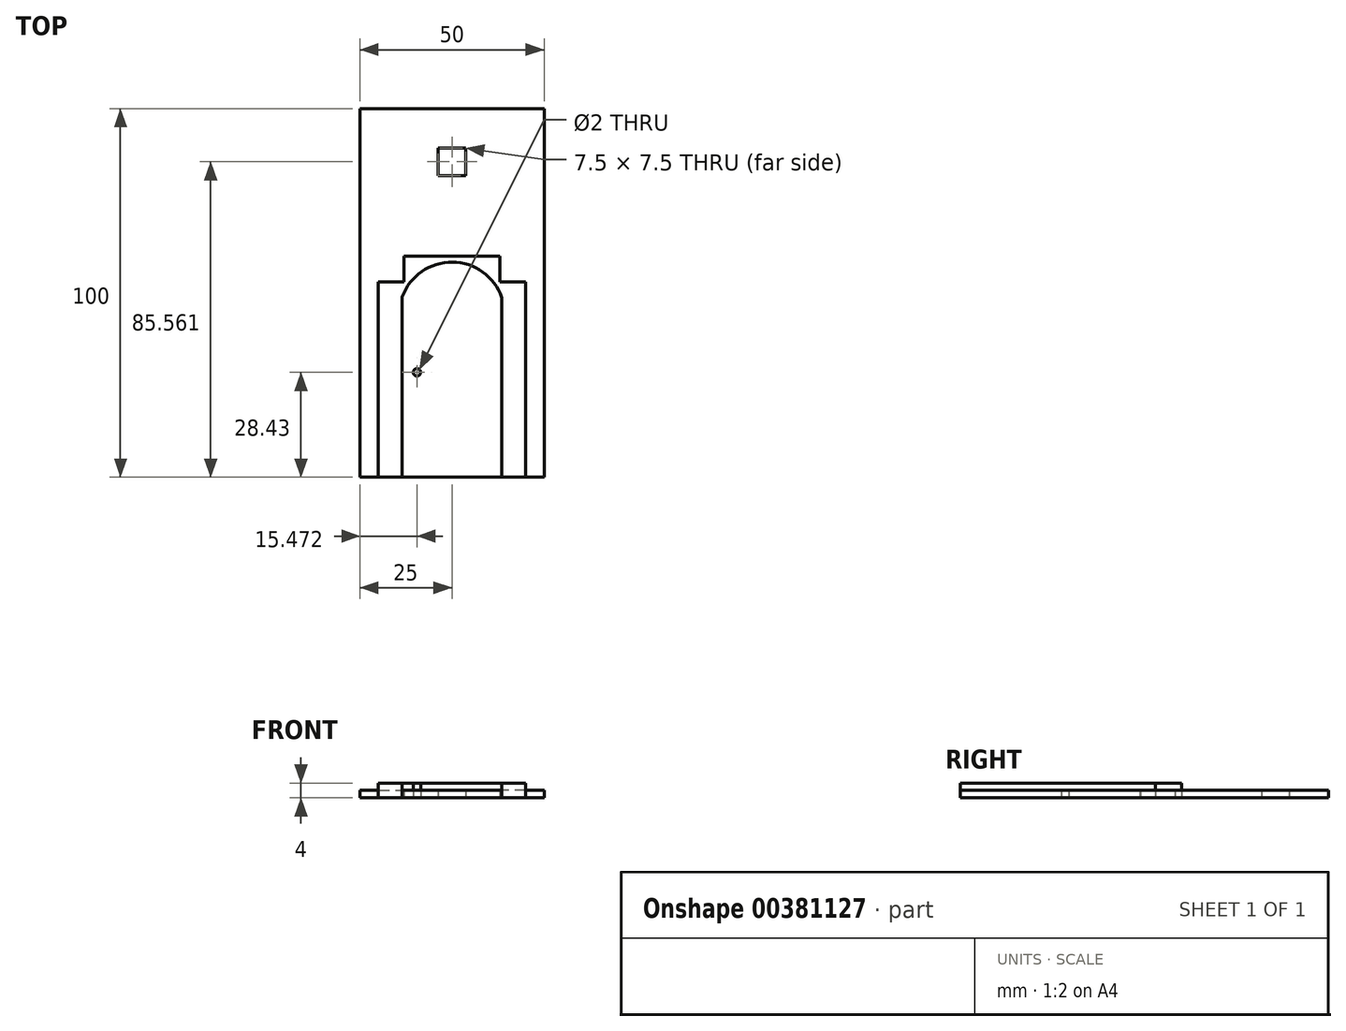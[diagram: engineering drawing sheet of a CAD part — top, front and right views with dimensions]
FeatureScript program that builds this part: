
annotation { "Feature Type Name" : "Feature", "Feature Type Description" : "" }
export const myFeature = defineFeature(function(context is Context, id is Id, definition is map)
    precondition{}
    {
        {
            var Q0;
            Q0=qCreatedBy(makeId("Top.planeOp"),FACE);
            var sketch = newSketch(context, id + "F0", { "sketchPlane" : qUnion([Q0])});
            skLineSegment(sketch, "E0.top", {"start": v(25, 50) * mm, "end": v(-25, 50) * mm});
            skLineSegment(sketch, "E0.left", {"start": v(25, -50) * mm, "end": v(25, 50) * mm});
            skLineSegment(sketch, "E0.right", {"start": v(-25, -50) * mm, "end": v(-25, 50) * mm});
            skPoint(sketch, "E0.middle", {"position": v(0, 0) * mm});
            skLineSegment(sketch, "E1.bottom", {"start": v(3.75, 31.81) * mm, "end": v(-3.75, 31.81) * mm});
            skLineSegment(sketch, "E1.top", {"start": v(3.75, 39.31) * mm, "end": v(-3.75, 39.31) * mm});
            skLineSegment(sketch, "E1.left", {"start": v(3.75, 31.81) * mm, "end": v(3.75, 39.31) * mm});
            skLineSegment(sketch, "E1.right", {"start": v(-3.75, 31.81) * mm, "end": v(-3.75, 39.31) * mm});
            skPoint(sketch, "E1.middle", {"position": v(0, 35.56) * mm});
            skLineSegment(sketch, "E2.left", {"start": v(-20, -50) * mm, "end": v(-20, 3) * mm});
            skLineSegment(sketch, "E2.right", {"start": v(20, -50) * mm, "end": v(20, 3) * mm});
            skLineSegment(sketch, "E3.top", {"start": v(-20, 3) * mm, "end": v(-20, 3) * mm});
            skLineSegment(sketch, "E3.right", {"start": v(-13, 10) * mm, "end": v(-13, 10) * mm});
            skLineSegment(sketch, "E4.top", {"start": v(20, 3) * mm, "end": v(13, 3) * mm});
            skLineSegment(sketch, "E4.right", {"start": v(13, 10) * mm, "end": v(13, 3) * mm});
            skLineSegment(sketch, "E5", {"start": v(-13, 10) * mm, "end": v(-13, 3) * mm});
            skLineSegment(sketch, "E6", {"start": v(-12.88, 10) * mm, "end": v(13, 10) * mm});
            skLineSegment(sketch, "E7", {"start": v(-20, 3) * mm, "end": v(-13, 3) * mm});
            skLineSegment(sketch, "E8.left", {"start": v(13.5, -50) * mm, "end": v(13.5, -1.3) * mm});
            skLineSegment(sketch, "E8.right", {"start": v(-13.5, -50) * mm, "end": v(-13.5, -1.06) * mm});
            skPoint(sketch, "E8.middle", {"position": v(0, -25) * mm});
            skArc(sketch, "E9", {"start": v(13.5, -1.3) * mm, "mid": v(13.25, -0.64) * mm, "end": v(12.98, 0) * mm});
            skArc(sketch, "E10", {"start": v(-13.06, 0) * mm, "mid": v(-13.3, -0.53) * mm, "end": v(-13.5, -1.06) * mm});
            skArc(sketch, "E11", {"start": v(12.98, 0) * mm, "mid": v(-0.04, 8.33) * mm, "end": v(-13.06, 0) * mm});
            skLineSegment(sketch, "E12", {"start": v(12.98, 0) * mm, "end": v(12.98, 0) * mm});
            skCircle(sketch, "E13", {"center": v(-9.53, -21.57) * mm, "radius": 1 * mm});
            skLineSegment(sketch, "E14", {"start": v(-13, 10) * mm, "end": v(-12.88, 10) * mm});
            skLineSegment(sketch, "E15", {"start": v(-25, -50) * mm, "end": v(25, -50) * mm});
            skSolve(sketch);
        }
        {
            var Q0;
            Q0=makeQuery(id+"F0.imprint","IMPRINT",FACE,{"disambiguationData":[TD([[makeQuery(id+"F0.imprint","IMPRINT",EDGE,{"derivedFrom":sQuery(id+"F0.wireOp",EDGE,"E0.top")}),1.0]])]});
            var Q1;
            Q1=makeQuery(id+"F0.imprint","IMPRINT",FACE,{"disambiguationData":[TD([[makeQuery(id+"F0.imprint","IMPRINT",EDGE,{"derivedFrom":sQuery(id+"F0.wireOp",EDGE,"E8.bottom")}),-1.0]])]});
            var Q2;
            {var subQ1=sQuery(id+"F0.wireOp",EDGE,"E8.left");Q2=makeQuery(id+"F0.imprint","IMPRINT",FACE,{"disambiguationData":[TD([[makeQuery(id+"F0.imprint","IMPRINT",EDGE,{"derivedFrom":subQ1}),1.0]])]});}
            extrude(context, id + "F1", {"entities" : qUnion([Q0, Q1, Q2]), "depth" : 2 * mm});
        }
        {
            var Q0;
            {var subQ1=sQuery(id+"F0.wireOp",EDGE,"E2.left");Q0=makeQuery(id+"F0.imprint","IMPRINT",FACE,{"disambiguationData":[TD([[makeQuery(id+"F0.imprint","IMPRINT",EDGE,{"derivedFrom":subQ1}),-1.0]])]});}
            var Q1;
            Q1=makeQuery(id+"F0.imprint","IMPRINT",FACE,{"disambiguationData":[TD([[makeQuery(id+"F0.imprint","IMPRINT",EDGE,{"derivedFrom":sQuery(id+"F0.wireOp",EDGE,"E13")}),1.0]])]});
            extrude(context, id + "F2", {"entities" : qUnion([Q0, Q1]), "depth" : 4 * mm});
        }
    });
